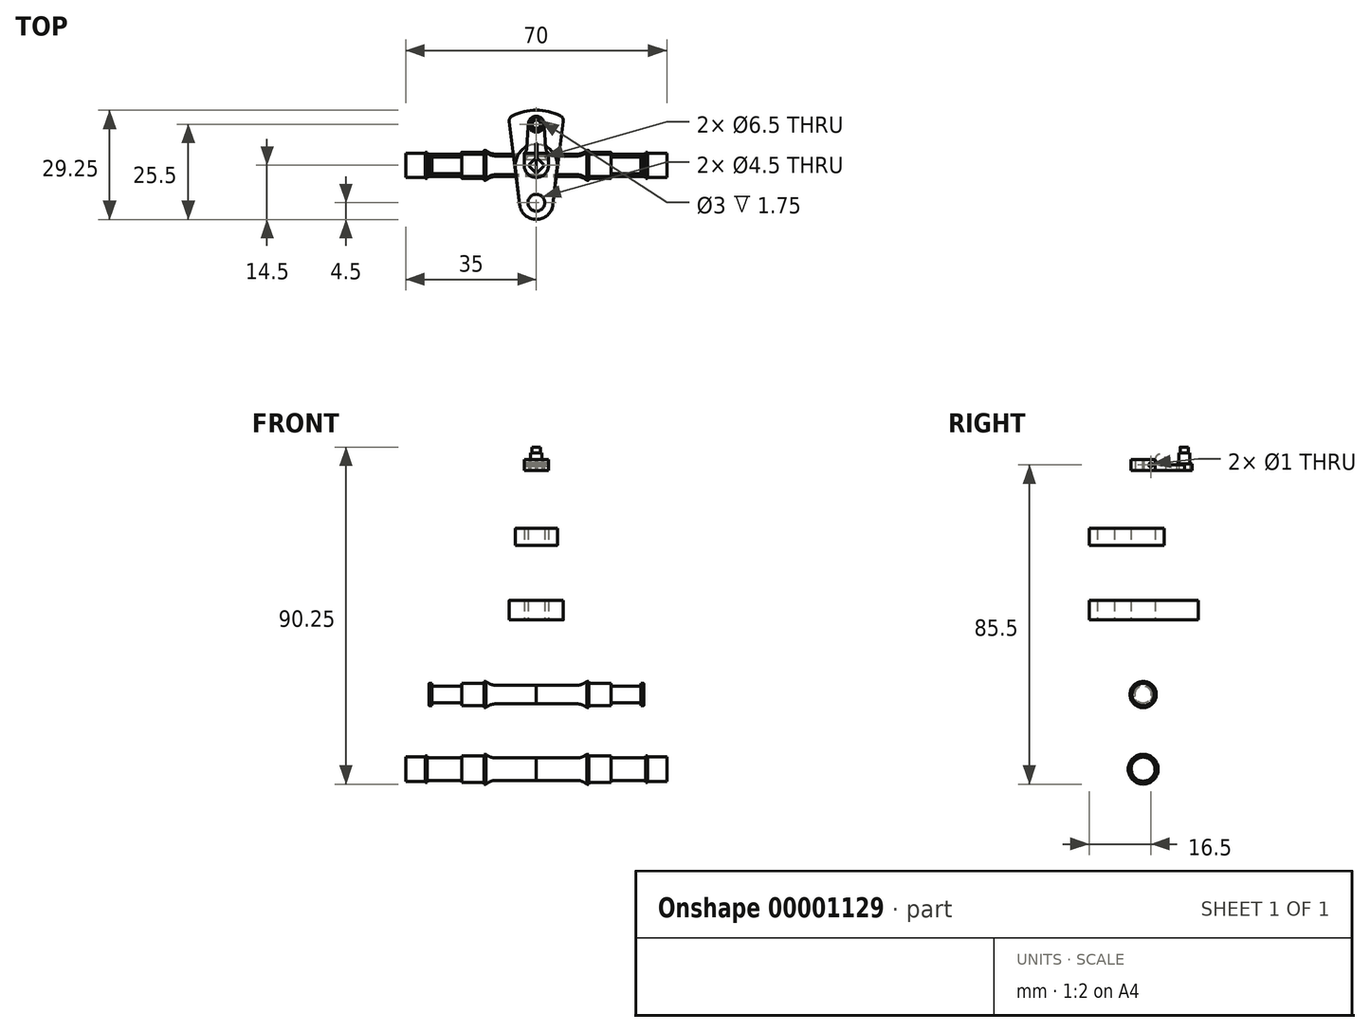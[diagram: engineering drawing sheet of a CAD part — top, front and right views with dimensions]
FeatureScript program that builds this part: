
annotation { "Feature Type Name" : "Feature", "Feature Type Description" : "" }
export const myFeature = defineFeature(function(context is Context, id is Id, definition is map)
    precondition{}
    {
        {
            var Q0;
            Q0=qCreatedBy(makeId("Top.planeOp"),FACE);
            var sketch = newSketch(context, id + "F0", { "sketchPlane" : qUnion([Q0])});
            skLineSegment(sketch, "E0", {"start": v(0, 0) * mm, "end": v(-28.75, 0) * mm, "construction": true});
            skLineSegment(sketch, "E1", {"start": v(-28.75, 0) * mm, "end": v(-28.75, 3) * mm});
            skLineSegment(sketch, "E2", {"start": v(-28.75, 3) * mm, "end": v(-28, 3) * mm});
            skLineSegment(sketch, "E3", {"start": v(-28, 3) * mm, "end": v(-28, 2.25) * mm});
            skLineSegment(sketch, "E4", {"start": v(-28, 2.25) * mm, "end": v(-20, 2.25) * mm});
            skLineSegment(sketch, "E5", {"start": v(-20, 2.25) * mm, "end": v(-20, 3) * mm});
            skLineSegment(sketch, "E6", {"start": v(-20, 3) * mm, "end": v(-14, 3) * mm});
            skLineSegment(sketch, "E7", {"start": v(-14, 3) * mm, "end": v(-14, 3.5) * mm});
            skLineSegment(sketch, "E8", {"start": v(-14, 3.5) * mm, "end": v(-13.5, 3.5) * mm});
            skLineSegment(sketch, "E9", {"start": v(-13.5, 3.5) * mm, "end": v(-13.5, 2.5) * mm});
            skLineSegment(sketch, "E10", {"start": v(0, 2.5) * mm, "end": v(0, 0) * mm});
            skLineSegment(sketch, "E11", {"start": v(-28.75, 0) * mm, "end": v(0, 0) * mm});
            skLineSegment(sketch, "E12", {"start": v(-13.5, 2.5) * mm, "end": v(0, 2.5) * mm});
            skSolve(sketch);
        }
        {
            var Q0;
            Q0=makeQuery(id+"F0.imprint","IMPRINT",FACE,{"disambiguationData":[TD([[makeQuery(id+"F0.imprint","IMPRINT",EDGE,{"derivedFrom":sQuery(id+"F0.wireOp",EDGE,"E1")}),-1.0]])]});
            var Q1;
            Q1=sQuery(id+"F0.wireOp",EDGE,"E11");
            revolve(context, id + "F1", {"entities" : qUnion([Q0]), "axis" : qUnion([Q1]), "revolveType" : RevolveType.FULL});
        }
        {
            var Q0;
            Q0=makeQuery(id+"F1.opRevolve","SWEPT_EDGE",EDGE,{"disambiguationData":[OSD([sQuery(id+"F0.wireOp",EDGE,"E9"),sQuery(id+"F0.wireOp",EDGE,"E12")])]});
            fillet(context, id + "F2", {"entities" : qUnion([Q0]), "radius" : 4 * mm, "tangentPropagation" : true, "allowEdgeOverflow" : false});
        }
        {
            var Q0;
            Q0=makeQuery(id+"F1.opRevolve","SWEPT_EDGE",EDGE,{"disambiguationData":[OSD([sQuery(id+"F0.wireOp",EDGE,"E1"),sQuery(id+"F0.wireOp",EDGE,"E2")])]});
            fillet(context, id + "F3", {"entities" : qUnion([Q0]), "radius" : 0.1 * mm, "tangentPropagation" : true, "allowEdgeOverflow" : false});
        }
        {
            var Q0;
            Q0=makeQuery(id+"F1.opRevolve","SWEPT_BODY",BODY,{"disambiguationData":[OSD([sQuery(id+"F0.wireOp",EDGE,"E1"),sQuery(id+"F0.wireOp",EDGE,"E2"),sQuery(id+"F0.wireOp",EDGE,"E3"),sQuery(id+"F0.wireOp",EDGE,"E4"),sQuery(id+"F0.wireOp",EDGE,"E5"),sQuery(id+"F0.wireOp",EDGE,"E6"),sQuery(id+"F0.wireOp",EDGE,"E7"),sQuery(id+"F0.wireOp",EDGE,"E8"),sQuery(id+"F0.wireOp",EDGE,"E9"),sQuery(id+"F0.wireOp",EDGE,"E10"),sQuery(id+"F0.wireOp",EDGE,"E11"),sQuery(id+"F0.wireOp",EDGE,"E12")])]});
            var Q1;
            Q1=makeQuery(id+"F1.opRevolve","SWEPT_FACE",FACE,{"disambiguationData":[OSD([sQuery(id+"F0.wireOp",EDGE,"E10")])]});
            mirror(context, id + "F4", {"entities" : qUnion([Q0]), "mirrorPlane" : qUnion([Q1])});
        }
        {
            var Q0;
            Q0=qCreatedBy(makeId("Top.planeOp"),FACE);
            cPlane(context, id + "F5", {"entities" : qUnion([Q0]), "cplaneType" : CPlaneType.OFFSET, "offset" : 20 * mm, "width" : 150 * mm, "height" : 150 * mm});
        }
        {
            var Q0;
            Q0=qCreatedBy(id+"F5.planeOp",FACE);
            var sketch = newSketch(context, id + "F6", { "sketchPlane" : qUnion([Q0])});
            skCircle(sketch, "E13", {"center": v(0, 0) * mm, "radius": 3.25 * mm});
            skCircle(sketch, "E14", {"center": v(0, -10) * mm, "radius": 2.25 * mm});
            skArc(sketch, "E15", {"start": v(-4.47, -10.56) * mm, "mid": v(0, -14.5) * mm, "end": v(4.47, -10.56) * mm});
            skLineSegment(sketch, "E16", {"start": v(7.25, 11.75) * mm, "end": v(4.47, -10.56) * mm});
            skArc(sketch, "E17", {"start": v(6.41, 13.28) * mm, "mid": v(0, 14.75) * mm, "end": v(-6.41, 13.28) * mm});
            skLineSegment(sketch, "E18", {"start": v(-7.25, 11.75) * mm, "end": v(-4.47, -10.56) * mm});
            skPoint(sketch, "E19.visualSharp", {"position": v(-7.38, 12.77) * mm});
            skArc(sketch, "E19.filletArc", {"start": v(-6.41, 13.28) * mm, "mid": v(-7.08, 12.65) * mm, "end": v(-7.25, 11.75) * mm});
            skPoint(sketch, "E20.visualSharp", {"position": v(7.38, 12.77) * mm});
            skArc(sketch, "E20.filletArc", {"start": v(7.25, 11.75) * mm, "mid": v(7.08, 12.65) * mm, "end": v(6.41, 13.28) * mm});
            skSolve(sketch);
        }
        {
            var Q0;
            Q0=makeQuery(id+"F6.imprint","IMPRINT",FACE,{"disambiguationData":[TD([[makeQuery(id+"F6.imprint","IMPRINT",EDGE,{"derivedFrom":sQuery(id+"F6.wireOp",EDGE,"E13")}),-1.0]])]});
            extrude(context, id + "F7", {"entities" : qUnion([Q0]), "depth" : 5.25 * mm});
        }
        {
            var Q0;
            Q0=qCreatedBy(id+"F5.planeOp",FACE);
            cPlane(context, id + "F8", {"entities" : qUnion([Q0]), "cplaneType" : CPlaneType.OFFSET, "offset" : 20 * mm, "width" : 150 * mm, "height" : 150 * mm});
        }
        {
            var Q0;
            Q0=qCreatedBy(id+"F8.planeOp",FACE);
            var sketch = newSketch(context, id + "F9", { "sketchPlane" : qUnion([Q0])});
            skCircle(sketch, "E21", {"center": v(0, 0) * mm, "radius": 3.25 * mm});
            skCircle(sketch, "E22", {"center": v(0, -10) * mm, "radius": 2.25 * mm});
            skArc(sketch, "E23", {"start": v(-4.47, -10.5) * mm, "mid": v(0, -14.5) * mm, "end": v(4.47, -10.5) * mm});
            skArc(sketch, "E24", {"start": v(5.59, -0.63) * mm, "mid": v(0, 5.62) * mm, "end": v(-5.59, -0.63) * mm});
            skLineSegment(sketch, "E25", {"start": v(-5.59, -0.63) * mm, "end": v(-4.47, -10.5) * mm});
            skLineSegment(sketch, "E26", {"start": v(4.47, -10.5) * mm, "end": v(5.59, -0.63) * mm});
            skSolve(sketch);
        }
        {
            var Q0;
            Q0=makeQuery(id+"F9.imprint","IMPRINT",FACE,{"disambiguationData":[TD([[makeQuery(id+"F9.imprint","IMPRINT",EDGE,{"derivedFrom":sQuery(id+"F9.wireOp",EDGE,"E21")}),-1.0]])]});
            extrude(context, id + "F10", {"entities" : qUnion([Q0]), "depth" : 4.5 * mm});
        }
        {
            var Q0;
            Q0=qCreatedBy(id+"F8.planeOp",FACE);
            cPlane(context, id + "F11", {"entities" : qUnion([Q0]), "cplaneType" : CPlaneType.OFFSET, "offset" : 20 * mm, "width" : 150 * mm, "height" : 150 * mm});
        }
        {
            var Q0;
            Q0=qCreatedBy(id+"F11.planeOp",FACE);
            var sketch = newSketch(context, id + "F12", { "sketchPlane" : qUnion([Q0])});
            skArc(sketch, "E27", {"start": v(-3.25, 0) * mm, "mid": v(0, -3.25) * mm, "end": v(3.25, 0) * mm});
            skCircle(sketch, "E28", {"center": v(0, 11) * mm, "radius": 2.12 * mm});
            skLineSegment(sketch, "E29", {"start": v(-3.25, 0) * mm, "end": v(-3.25, 3.25) * mm});
            skLineSegment(sketch, "E30", {"start": v(-3.25, 3.25) * mm, "end": v(-2.62, 3.25) * mm});
            skLineSegment(sketch, "E31", {"start": v(-2.63, 3.25) * mm, "end": v(-2.12, 11.14) * mm});
            skLineSegment(sketch, "E32", {"start": v(3.25, 0) * mm, "end": v(3.25, 3.25) * mm});
            skLineSegment(sketch, "E33", {"start": v(3.25, 3.25) * mm, "end": v(2.62, 3.25) * mm});
            skLineSegment(sketch, "E34", {"start": v(2.63, 3.25) * mm, "end": v(2.12, 11.14) * mm});
            skCircle(sketch, "E35", {"center": v(0, 11) * mm, "radius": 1.5 * mm});
            skCircle(sketch, "E36.cCircle", {"center": v(0, 0) * mm, "radius": 1.5 * mm, "construction": true});
            skLineSegment(sketch, "E36.0", {"start": v(0, 2.12) * mm, "end": v(2.12, 0) * mm});
            skLineSegment(sketch, "E36.1", {"start": v(2.12, 0) * mm, "end": v(0, -2.12) * mm});
            skLineSegment(sketch, "E36.2", {"start": v(0, -2.12) * mm, "end": v(-2.12, 0) * mm});
            skLineSegment(sketch, "E36.3", {"start": v(-2.12, 0) * mm, "end": v(0, 2.12) * mm});
            skPoint(sketch, "E36.0.midPoint", {"position": v(1.06, 1.06) * mm});
            skSolve(sketch);
        }
        {
            var Q0;
            Q0=makeQuery(id+"F12.imprint","IMPRINT",FACE,{"disambiguationData":[TD([[makeQuery(id+"F12.imprint","IMPRINT",EDGE,{"derivedFrom":sQuery(id+"F12.wireOp",EDGE,"E27")}),1.0]])]});
            extrude(context, id + "F13", {"entities" : qUnion([Q0]), "depth" : 3 * mm});
        }
        {
            var Q0;
            Q0=makeQuery(id+"F13.opExtrude","SWEPT_EDGE",EDGE,{"disambiguationData":[OSD([sQuery(id+"F12.wireOp",EDGE,"E30"),sQuery(id+"F12.wireOp",EDGE,"E31")])]});
            var Q1;
            Q1=makeQuery(id+"F13.opExtrude","SWEPT_EDGE",EDGE,{"disambiguationData":[OSD([sQuery(id+"F12.wireOp",EDGE,"E33"),sQuery(id+"F12.wireOp",EDGE,"E34")])]});
            fillet(context, id + "F14", {"entities" : qUnion([Q0, Q1]), "radius" : 2 * mm, "tangentPropagation" : true, "allowEdgeOverflow" : false});
        }
        {
            var Q0;
            Q0=makeQuery(id+"F13.opExtrude","SWEPT_FACE",FACE,{"disambiguationData":[OSD([sQuery(id+"F12.wireOp",EDGE,"E29")])]});
            var sketch = newSketch(context, id + "F15", { "sketchPlane" : qUnion([Q0])});
            skArc(sketch, "E37", {"start": v(-4.65, 61.6) * mm, "mid": v(-3.66, 62.01) * mm, "end": v(-3.25, 63) * mm});
            skLineSegment(sketch, "E38", {"start": v(-4.65, 61.6) * mm, "end": v(-13.78, 61.6) * mm});
            skLineSegment(sketch, "E39", {"start": v(-13.78, 63) * mm, "end": v(-13.78, 61.6) * mm});
            skLineSegment(sketch, "E40", {"start": v(-3.25, 63) * mm, "end": v(-13.78, 63) * mm});
            skSolve(sketch);
        }
        {
            var Q0;
            Q0=makeQuery(id+"F12.imprint","IMPRINT",FACE,{"disambiguationData":[TD([[makeQuery(id+"F12.imprint","IMPRINT",EDGE,{"derivedFrom":sQuery(id+"F12.wireOp",EDGE,"E35")}),1.0]])]});
            extrude(context, id + "F16", {"entities" : qUnion([Q0]), "depth" : 4.75 * mm});
        }
        {
            var Q0;
            Q0=makeQuery(id+"F12.imprint","IMPRINT",FACE,{"disambiguationData":[TD([[makeQuery(id+"F12.imprint","IMPRINT",EDGE,{"derivedFrom":sQuery(id+"F12.wireOp",EDGE,"E35")}),-1.0]])]});
            extrude(context, id + "F17", {"entities" : qUnion([Q0]), "depth" : 1.75 * mm});
        }
        {
            var Q0;
            Q0=makeQuery(id+"F15.imprint","IMPRINT",FACE,{"disambiguationData":[TD([[makeQuery(id+"F15.imprint","IMPRINT",EDGE,{"derivedFrom":sQuery(id+"F15.wireOp",EDGE,"E37")}),1.0]])]});
            extrude(context, id + "F18", {"entities" : qUnion([Q0]), "oppositeDirection" : true, "depth" : 8 * mm});
        }
        {
            var Q0;
            Q0=makeQuery(id+"F18.opExtrude","SWEPT_BODY",BODY,{"disambiguationData":[OSD([sQuery(id+"F15.wireOp",EDGE,"E37"),sQuery(id+"F15.wireOp",EDGE,"E38"),sQuery(id+"F15.wireOp",EDGE,"E39"),sQuery(id+"F15.wireOp",EDGE,"E40")])]});
            var Q1;
            Q1=makeQuery(id+"F13.opExtrude","SWEPT_BODY",BODY,{"disambiguationData":[OSD([sQuery(id+"F12.wireOp",EDGE,"E27"),sQuery(id+"F12.wireOp",EDGE,"E28"),sQuery(id+"F12.wireOp",EDGE,"E29"),sQuery(id+"F12.wireOp",EDGE,"E30"),sQuery(id+"F12.wireOp",EDGE,"E31"),sQuery(id+"F12.wireOp",EDGE,"E32"),sQuery(id+"F12.wireOp",EDGE,"E33"),sQuery(id+"F12.wireOp",EDGE,"E34"),sQuery(id+"F12.wireOp",EDGE,"E36.0"),sQuery(id+"F12.wireOp",EDGE,"E36.1"),sQuery(id+"F12.wireOp",EDGE,"E36.2"),sQuery(id+"F12.wireOp",EDGE,"E36.3")])]});
            booleanBodies(context, id + "F19", {"operationType" : BooleanOperationType.SUBTRACTION, "tools" : qUnion([Q0]), "targets" : qUnion([Q1])});
        }
        {
            var Q0;
            Q0=makeQuery(id+"F19.opBoolean","INTERSECT",EDGE,{"derivedFrom":[makeQuery(id+"F13.opExtrude","SWEPT_FACE",FACE,{"disambiguationData":[OSD([sQuery(id+"F12.wireOp",EDGE,"E28")])]}),makeQuery(id+"F18.opExtrude","SWEPT_FACE",FACE,{"disambiguationData":[OSD([sQuery(id+"F15.wireOp",EDGE,"E38")])]})]});
            fillet(context, id + "F20", {"entities" : qUnion([Q0]), "radius" : 0.15 * mm, "tangentPropagation" : true, "allowEdgeOverflow" : false});
        }
        {
            var Q0;
            Q0=makeQuery(id+"F13.opExtrude","SWEPT_EDGE",EDGE,{"disambiguationData":[OSD([sQuery(id+"F12.wireOp",EDGE,"E36.2"),sQuery(id+"F12.wireOp",EDGE,"E36.3")])]});
            var Q1;
            Q1=makeQuery(id+"F13.opExtrude","SWEPT_EDGE",EDGE,{"disambiguationData":[OSD([sQuery(id+"F12.wireOp",EDGE,"E36.1"),sQuery(id+"F12.wireOp",EDGE,"E36.2")])]});
            var Q2;
            Q2=makeQuery(id+"F13.opExtrude","SWEPT_EDGE",EDGE,{"disambiguationData":[OSD([sQuery(id+"F12.wireOp",EDGE,"E36.0"),sQuery(id+"F12.wireOp",EDGE,"E36.1")])]});
            var Q3;
            Q3=makeQuery(id+"F13.opExtrude","SWEPT_EDGE",EDGE,{"disambiguationData":[OSD([sQuery(id+"F12.wireOp",EDGE,"E36.0"),sQuery(id+"F12.wireOp",EDGE,"E36.3")])]});
            chamfer(context, id + "F21", {"entities" : qUnion([Q0, Q1, Q2, Q3]), "width" : 0.25 * mm, "tangentPropagation" : true});
        }
        {
            var Q0;
            Q0=makeQuery(id+"F21.opChamfer","BLEND_FACE",FACE,{"disambiguationData":[OSD([sQuery(id+"F12.wireOp",EDGE,"E36.0"),sQuery(id+"F12.wireOp",EDGE,"E36.3")])]});
            extrude(context, id + "F22", {"entities" : qUnion([Q0]), "operationType" : NewBodyOperationType.REMOVE, "oppositeDirection" : true, "depth" : 4 * mm});
        }
        {
            var Q0;
            {var subQ0=sQuery(id+"F12.wireOp",EDGE,"E36.0");var subQ1=sQuery(id+"F12.wireOp",EDGE,"E36.3");Q0=makeQuery(id+"F22.boolean.opBoolean","COPY",EDGE,{"derivedFrom":makeQuery(id+"F22.opExtrude","CAP_EDGE",EDGE,{"disambiguationData":[OSD([subQ0,subQ1]),TDD([makeQuery(id+"F21.opChamfer","BLEND_EDGE",EDGE,{"blendedFrom":[makeQuery(id+"F13.opExtrude","SWEPT_EDGE",EDGE,{"disambiguationData":[OSD([subQ0,subQ1])]}),makeQuery(id+"F13.opExtrude","SWEPT_FACE",FACE,{"disambiguationData":[OSD([subQ1])]})],"blendedInto":[makeQuery(id+"F13.opExtrude","SWEPT_FACE",FACE,{"disambiguationData":[OSD([subQ1])]})]})])],"isStart":false})});}
            var Q1;
            {var subQ0=sQuery(id+"F12.wireOp",EDGE,"E36.0");var subQ1=sQuery(id+"F12.wireOp",EDGE,"E36.3");Q1=makeQuery(id+"F22.boolean.opBoolean","COPY",EDGE,{"derivedFrom":makeQuery(id+"F22.opExtrude","CAP_EDGE",EDGE,{"disambiguationData":[OSD([subQ0,subQ1]),TDD([makeQuery(id+"F21.opChamfer","BLEND_EDGE",EDGE,{"blendedFrom":[makeQuery(id+"F13.opExtrude","SWEPT_EDGE",EDGE,{"disambiguationData":[OSD([subQ0,subQ1])]}),makeQuery(id+"F13.opExtrude","SWEPT_FACE",FACE,{"disambiguationData":[OSD([subQ0])]})],"blendedInto":[makeQuery(id+"F13.opExtrude","SWEPT_FACE",FACE,{"disambiguationData":[OSD([subQ0])]})]})])],"isStart":false})});}
            fillet(context, id + "F23", {"entities" : qUnion([Q0, Q1]), "radius" : 0.12 * mm, "tangentPropagation" : true, "allowEdgeOverflow" : false});
        }
        {
            var Q0;
            Q0=makeQuery(id+"F16.opExtrude","CAP_FACE",FACE,{"disambiguationData":[OSD([sQuery(id+"F12.wireOp",EDGE,"E35")])],"isStart":false});
            var sketch = newSketch(context, id + "F24", { "sketchPlane" : qUnion([Q0])});
            skCircle(sketch, "E41", {"center": v(0, 11) * mm, "radius": 1.13 * mm});
            skSolve(sketch);
        }
        {
            var Q0;
            Q0=makeQuery(id+"F24.imprint","IMPRINT",FACE,{"disambiguationData":[TD([[makeQuery(id+"F24.imprint","IMPRINT",EDGE,{"derivedFrom":sQuery(id+"F24.wireOp",EDGE,"E41")}),1.0]])]});
            extrude(context, id + "F25", {"entities" : qUnion([Q0]), "operationType" : NewBodyOperationType.ADD, "depth" : 1.5 * mm});
        }
        {
            var Q0;
            Q0=makeQuery(id+"F13.opExtrude","SWEPT_FACE",FACE,{"disambiguationData":[OSD([sQuery(id+"F12.wireOp",EDGE,"E29")])]});
            var sketch = newSketch(context, id + "F26", { "sketchPlane" : qUnion([Q0])});
            skLineSegment(sketch, "E42", {"start": v(0, 61.5) * mm, "end": v(-3.25, 61.5) * mm, "construction": true});
            skCircle(sketch, "E43", {"center": v(-2, 61.5) * mm, "radius": 0.5 * mm});
            skSolve(sketch);
        }
        {
            var Q0;
            Q0=makeQuery(id+"F26.imprint","IMPRINT",FACE,{"disambiguationData":[TD([[makeQuery(id+"F26.imprint","IMPRINT",EDGE,{"derivedFrom":sQuery(id+"F26.wireOp",EDGE,"E43")}),1.0]])]});
            extrude(context, id + "F27", {"entities" : qUnion([Q0]), "operationType" : NewBodyOperationType.REMOVE, "oppositeDirection" : true, "depth" : 25 * mm});
        }
        {
            var Q0;
            Q0=qCreatedBy(makeId("Top.planeOp"),FACE);
            cPlane(context, id + "F28", {"entities" : qUnion([Q0]), "cplaneType" : CPlaneType.OFFSET, "offset" : 20 * mm, "oppositeDirection" : true, "width" : 150 * mm, "height" : 150 * mm});
        }
        {
            var Q0;
            Q0=qCreatedBy(id+"F28.planeOp",FACE);
            var sketch = newSketch(context, id + "F29", { "sketchPlane" : qUnion([Q0])});
            skLineSegment(sketch, "E44", {"start": v(0, 0) * mm, "end": v(0, 3) * mm});
            skLineSegment(sketch, "E45", {"start": v(0, 3) * mm, "end": v(13.5, 3) * mm});
            skLineSegment(sketch, "E46", {"start": v(13.5, 3) * mm, "end": v(13.5, 4) * mm});
            skLineSegment(sketch, "E47", {"start": v(13.5, 4) * mm, "end": v(14, 4) * mm});
            skLineSegment(sketch, "E48", {"start": v(14, 4) * mm, "end": v(14, 3.5) * mm});
            skLineSegment(sketch, "E49", {"start": v(14, 3.5) * mm, "end": v(20, 3.5) * mm});
            skLineSegment(sketch, "E50", {"start": v(20, 3.5) * mm, "end": v(20, 3) * mm});
            skLineSegment(sketch, "E51", {"start": v(20, 3) * mm, "end": v(29.25, 3) * mm});
            skLineSegment(sketch, "E52", {"start": v(29.25, 3) * mm, "end": v(29.25, 3.5) * mm});
            skLineSegment(sketch, "E53", {"start": v(29.25, 3.5) * mm, "end": v(29.75, 3.5) * mm});
            skLineSegment(sketch, "E54", {"start": v(29.75, 3.5) * mm, "end": v(29.75, 3.25) * mm});
            skLineSegment(sketch, "E55", {"start": v(29.75, 3.25) * mm, "end": v(35, 3.25) * mm});
            skLineSegment(sketch, "E56", {"start": v(35, 3.25) * mm, "end": v(35, 0) * mm});
            skLineSegment(sketch, "E57", {"start": v(35, 0) * mm, "end": v(0, 0) * mm});
            skSolve(sketch);
        }
        {
            var Q0;
            Q0=makeQuery(id+"F29.imprint","IMPRINT",FACE,{"disambiguationData":[TD([[makeQuery(id+"F29.imprint","IMPRINT",EDGE,{"derivedFrom":sQuery(id+"F29.wireOp",EDGE,"E44")}),-1.0]])]});
            var Q1;
            Q1=sQuery(id+"F29.wireOp",EDGE,"E57");
            revolve(context, id + "F30", {"entities" : qUnion([Q0]), "axis" : qUnion([Q1]), "revolveType" : RevolveType.FULL});
        }
        {
            var Q0;
            Q0=makeQuery(id+"F30.opRevolve","SWEPT_EDGE",EDGE,{"disambiguationData":[OSD([sQuery(id+"F29.wireOp",EDGE,"E45"),sQuery(id+"F29.wireOp",EDGE,"E46")])]});
            fillet(context, id + "F31", {"entities" : qUnion([Q0]), "radius" : 4 * mm, "tangentPropagation" : true, "allowEdgeOverflow" : false});
        }
        {
            var Q0;
            Q0=makeQuery(id+"F30.opRevolve","SWEPT_BODY",BODY,{"disambiguationData":[OSD([sQuery(id+"F29.wireOp",EDGE,"E44"),sQuery(id+"F29.wireOp",EDGE,"E45"),sQuery(id+"F29.wireOp",EDGE,"E46"),sQuery(id+"F29.wireOp",EDGE,"E47"),sQuery(id+"F29.wireOp",EDGE,"E48"),sQuery(id+"F29.wireOp",EDGE,"E49"),sQuery(id+"F29.wireOp",EDGE,"E50"),sQuery(id+"F29.wireOp",EDGE,"E51"),sQuery(id+"F29.wireOp",EDGE,"E52"),sQuery(id+"F29.wireOp",EDGE,"E53"),sQuery(id+"F29.wireOp",EDGE,"E54"),sQuery(id+"F29.wireOp",EDGE,"E55"),sQuery(id+"F29.wireOp",EDGE,"E56"),sQuery(id+"F29.wireOp",EDGE,"E57")])]});
            var Q1;
            Q1=makeQuery(id+"F30.opRevolve","SWEPT_FACE",FACE,{"disambiguationData":[OSD([sQuery(id+"F29.wireOp",EDGE,"E44")])]});
            mirror(context, id + "F32", {"entities" : qUnion([Q0]), "mirrorPlane" : qUnion([Q1])});
        }
    });
